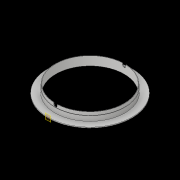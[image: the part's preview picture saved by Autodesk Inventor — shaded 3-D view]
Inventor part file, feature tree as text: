
AUTODESK INVENTOR PART (.ipt)
format: ipt  version: 2017 (Build 210142000, 142)  size: 138,752 bytes
history: native  units: in
note: dims shown in document units (in); Inventor stores cm internally (conversion verified against a paired STEP export)
features: sketch x2, revolve x1, plane x1, extrude x1
ambient origin geometry x8: Origin, YZ Plane, XZ Plane, XY Plane, X Axis, Y Axis, Z Axis, Center Point
bodies: Solid1 (feature_tree)
feature tree (5):
  revolve  "Revolution1"  [1 undecoded]
  plane  "Work Plane2"
  extrude  "Extrusion2"  Depth=0.125in
  sketch  "Sketch1"  dims[d0=2.0in d1=5.4375in]
  sketch  "Sketch3"  dims[d2=1.25in d3=0.125in d4=0.125in d5=2.25in d6=1.5in d7=0.125in d8=90.0deg d13=1.0285in d14=0.0625in d15=0.25in d16=0.25in d17=1.0in d18=0.0in]
note: 1 required parameter value undecoded (feature->parameter linkage not recoverable at this tier; creation-order binding heuristic only, values carry confidence <= 0.55)
